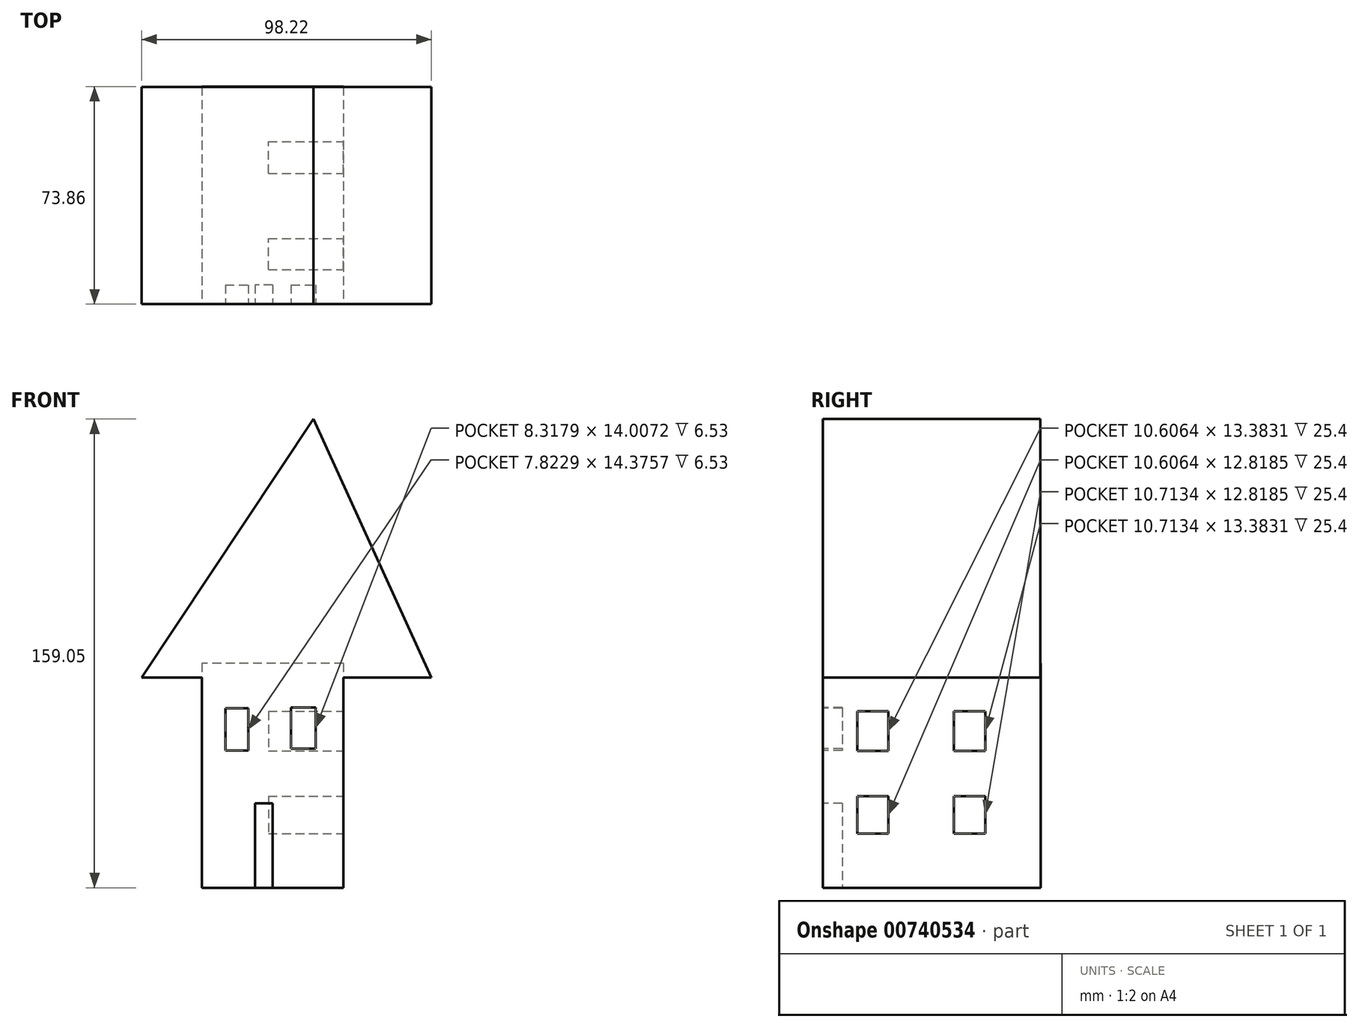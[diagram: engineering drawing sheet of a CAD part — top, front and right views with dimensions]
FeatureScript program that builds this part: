
annotation { "Feature Type Name" : "Feature", "Feature Type Description" : "" }
export const myFeature = defineFeature(function(context is Context, id is Id, definition is map)
    precondition{}
    {
        {
            var Q0;
            Q0=qCreatedBy(makeId("Top.planeOp"),FACE);
            var sketch = newSketch(context, id + "F0", { "sketchPlane" : qUnion([Q0])});
            skLineSegment(sketch, "E0.bottom", {"start": v(47.9, 51.6) * mm, "end": v(0, 51.6) * mm});
            skLineSegment(sketch, "E0.top", {"start": v(47.9, -22.26) * mm, "end": v(0, -22.26) * mm});
            skLineSegment(sketch, "E0.left", {"start": v(47.9, 51.6) * mm, "end": v(47.9, -22.26) * mm});
            skLineSegment(sketch, "E0.right", {"start": v(0, 51.6) * mm, "end": v(0, -22.26) * mm});
            skSolve(sketch);
        }
        {
            var Q0;
            Q0 = qSketchRegion(id + "F0", true);
            extrude(context, id + "F1", {"entities" : qUnion([Q0]), "depth" : 76.2 * mm, "offsetDistance" : 25.4 * mm});
        }
        {
            var Q0;
            Q0=makeQuery(id+"F1.opExtrude","SWEPT_FACE",FACE,{"disambiguationData":[OSD([sQuery(id+"F0.wireOp",EDGE,"E0.top")])]});
            var sketch = newSketch(context, id + "F2", { "sketchPlane" : qUnion([Q0])});
            skLineSegment(sketch, "E1", {"start": v(-20.45, 71.34) * mm, "end": v(77.77, 71.34) * mm});
            skLineSegment(sketch, "E2", {"start": v(77.77, 71.34) * mm, "end": v(37.76, 159.05) * mm});
            skLineSegment(sketch, "E3", {"start": v(37.76, 159.05) * mm, "end": v(-20.45, 71.34) * mm});
            skSolve(sketch);
        }
        {
            var Q0;
            {var subQ1=sQuery(id+"F2.wireOp",EDGE,"E2");Q0=makeQuery(id+"F2.imprint","IMPRINT",FACE,{"disambiguationData":[TD([[makeQuery(id+"F2.imprint","IMPRINT",EDGE,{"derivedFrom":subQ1}),1.0]])]});}
            extrude(context, id + "F3", {"entities" : qUnion([Q0]), "operationType" : NewBodyOperationType.ADD, "oppositeDirection" : true, "depth" : 73.73 * mm, "offsetDistance" : 25.4 * mm});
        }
        {
            var Q0;
            {var subQ0=sQuery(id+"F0.wireOp",EDGE,"E0.top");Q0=makeQuery(id+"F3.boolean.opBoolean","MERGE",FACE,{"derivedFrom":[makeQuery(id+"F1.opExtrude","SWEPT_FACE",FACE,{"disambiguationData":[OSD([subQ0])]}),makeQuery(id+"F3.opExtrude","CAP_FACE",FACE,{"disambiguationData":[OSD([subQ0,sQuery(id+"F0.wireOp",EDGE,"E0.left"),sQuery(id+"F0.wireOp",EDGE,"E0.right"),sQuery(id+"F2.wireOp",EDGE,"E1"),sQuery(id+"F2.wireOp",EDGE,"E2"),sQuery(id+"F2.wireOp",EDGE,"E3")])],"isStart":true})]});}
            var sketch = newSketch(context, id + "F4", { "sketchPlane" : qUnion([Q0])});
            skLineSegment(sketch, "E4.bottom", {"start": v(7.9, 60.92) * mm, "end": v(15.71, 60.92) * mm});
            skLineSegment(sketch, "E4.top", {"start": v(7.9, 46.54) * mm, "end": v(15.71, 46.54) * mm});
            skLineSegment(sketch, "E4.left", {"start": v(7.9, 60.92) * mm, "end": v(7.9, 46.54) * mm});
            skLineSegment(sketch, "E4.right", {"start": v(15.71, 60.92) * mm, "end": v(15.71, 46.54) * mm});
            skLineSegment(sketch, "E5.bottom", {"start": v(30.22, 61.18) * mm, "end": v(38.54, 61.18) * mm});
            skLineSegment(sketch, "E5.top", {"start": v(30.22, 47.17) * mm, "end": v(38.54, 47.17) * mm});
            skLineSegment(sketch, "E5.left", {"start": v(30.22, 61.18) * mm, "end": v(30.22, 47.17) * mm});
            skLineSegment(sketch, "E5.right", {"start": v(38.54, 61.18) * mm, "end": v(38.54, 47.17) * mm});
            skLineSegment(sketch, "E6.bottom", {"start": v(17.92, 28.67) * mm, "end": v(23.95, 28.67) * mm});
            skLineSegment(sketch, "E6.top", {"start": v(17.92, 0) * mm, "end": v(23.95, 0) * mm});
            skLineSegment(sketch, "E6.left", {"start": v(17.92, 28.67) * mm, "end": v(17.92, 0) * mm});
            skLineSegment(sketch, "E6.right", {"start": v(23.95, 28.67) * mm, "end": v(23.95, 0) * mm});
            skSolve(sketch);
        }
        {
            var Q0;
            Q0=makeQuery(id+"F4.imprint","IMPRINT",FACE,{"disambiguationData":[TD([[makeQuery(id+"F4.imprint","IMPRINT",EDGE,{"derivedFrom":sQuery(id+"F4.wireOp",EDGE,"E4.bottom")}),-1.0]])]});
            var Q1;
            Q1=makeQuery(id+"F4.imprint","IMPRINT",FACE,{"disambiguationData":[TD([[makeQuery(id+"F4.imprint","IMPRINT",EDGE,{"derivedFrom":sQuery(id+"F4.wireOp",EDGE,"E5.bottom")}),-1.0]])]});
            var Q2;
            Q2=makeQuery(id+"F4.imprint","IMPRINT",FACE,{"disambiguationData":[TD([[makeQuery(id+"F4.imprint","IMPRINT",EDGE,{"derivedFrom":sQuery(id+"F4.wireOp",EDGE,"E6.bottom")}),-1.0]])]});
            extrude(context, id + "F5", {"entities" : qUnion([Q0, Q1, Q2]), "operationType" : NewBodyOperationType.REMOVE, "oppositeDirection" : true, "depth" : 6.53 * mm, "offsetDistance" : 25.4 * mm});
        }
        {
            var Q0;
            Q0=makeQuery(id+"F1.opExtrude","SWEPT_FACE",FACE,{"disambiguationData":[OSD([sQuery(id+"F0.wireOp",EDGE,"E0.left")])]});
            var sketch = newSketch(context, id + "F6", { "sketchPlane" : qUnion([Q0])});
            skLineSegment(sketch, "E7.bottom", {"start": v(-10.6, 59.87) * mm, "end": v(0, 59.87) * mm});
            skLineSegment(sketch, "E7.top", {"start": v(-10.6, 46.49) * mm, "end": v(0, 46.49) * mm});
            skLineSegment(sketch, "E7.left", {"start": v(-10.6, 59.87) * mm, "end": v(-10.6, 46.49) * mm});
            skLineSegment(sketch, "E7.right", {"start": v(0, 59.87) * mm, "end": v(0, 46.49) * mm});
            skLineSegment(sketch, "E8.bottom", {"start": v(22.15, 59.87) * mm, "end": v(32.86, 59.87) * mm});
            skLineSegment(sketch, "E8.top", {"start": v(22.15, 46.49) * mm, "end": v(32.86, 46.49) * mm});
            skLineSegment(sketch, "E8.left", {"start": v(22.15, 59.87) * mm, "end": v(22.15, 46.49) * mm});
            skLineSegment(sketch, "E8.right", {"start": v(32.86, 59.87) * mm, "end": v(32.86, 46.49) * mm});
            skLineSegment(sketch, "E9.bottom", {"start": v(-10.6, 31.13) * mm, "end": v(0, 31.13) * mm});
            skLineSegment(sketch, "E9.top", {"start": v(-10.6, 18.3) * mm, "end": v(0, 18.3) * mm});
            skLineSegment(sketch, "E9.left", {"start": v(-10.6, 31.13) * mm, "end": v(-10.6, 18.3) * mm});
            skLineSegment(sketch, "E9.right", {"start": v(0, 31.13) * mm, "end": v(0, 18.3) * mm});
            skLineSegment(sketch, "E10.bottom", {"start": v(22.15, 31.13) * mm, "end": v(32.86, 31.13) * mm});
            skLineSegment(sketch, "E10.top", {"start": v(22.15, 18.3) * mm, "end": v(32.86, 18.3) * mm});
            skLineSegment(sketch, "E10.left", {"start": v(22.15, 31.13) * mm, "end": v(22.15, 18.3) * mm});
            skLineSegment(sketch, "E10.right", {"start": v(32.86, 31.13) * mm, "end": v(32.86, 18.3) * mm});
            skSolve(sketch);
        }
        {
            var Q0;
            Q0=makeQuery(id+"F6.imprint","IMPRINT",FACE,{"disambiguationData":[TD([[makeQuery(id+"F6.imprint","IMPRINT",EDGE,{"derivedFrom":sQuery(id+"F6.wireOp",EDGE,"E7.bottom")}),-1.0]])]});
            var Q1;
            Q1=makeQuery(id+"F6.imprint","IMPRINT",FACE,{"disambiguationData":[TD([[makeQuery(id+"F6.imprint","IMPRINT",EDGE,{"derivedFrom":sQuery(id+"F6.wireOp",EDGE,"E9.bottom")}),-1.0]])]});
            var Q2;
            Q2=makeQuery(id+"F6.imprint","IMPRINT",FACE,{"disambiguationData":[TD([[makeQuery(id+"F6.imprint","IMPRINT",EDGE,{"derivedFrom":sQuery(id+"F6.wireOp",EDGE,"E10.bottom")}),-1.0]])]});
            var Q3;
            Q3=makeQuery(id+"F6.imprint","IMPRINT",FACE,{"disambiguationData":[TD([[makeQuery(id+"F6.imprint","IMPRINT",EDGE,{"derivedFrom":sQuery(id+"F6.wireOp",EDGE,"E8.bottom")}),-1.0]])]});
            extrude(context, id + "F7", {"entities" : qUnion([Q0, Q1, Q2, Q3]), "operationType" : NewBodyOperationType.REMOVE, "oppositeDirection" : true, "depth" : 25.4 * mm, "offsetDistance" : 25.4 * mm});
        }
    });
